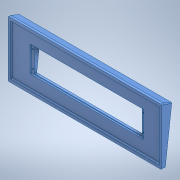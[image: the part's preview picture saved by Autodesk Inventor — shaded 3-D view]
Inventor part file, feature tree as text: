
AUTODESK INVENTOR PART (.ipt)
format: ipt  version: 2020 (Build 240168000, 168)  size: 145,408 bytes
history: mixed  units: mm
features: fillet x1, imported_body x1
ambient origin geometry x8: Origin, YZ Plane, XZ Plane, XY Plane, X Axis, Y Axis, Z Axis, Center Point
bodies: Solid1 (imported_parasolid)
feature tree (2):
  fillet  "Fillet2"  [1 undecoded]
  imported_body  NMx_Import_Brep_tag  [imported B-rep: ~47 faces, bbox_mm=[356.6125, 131.1125, 23.543677]]
note: 1 required parameter value undecoded (feature->parameter linkage not recoverable at this tier; creation-order binding heuristic only, values carry confidence <= 0.55)
